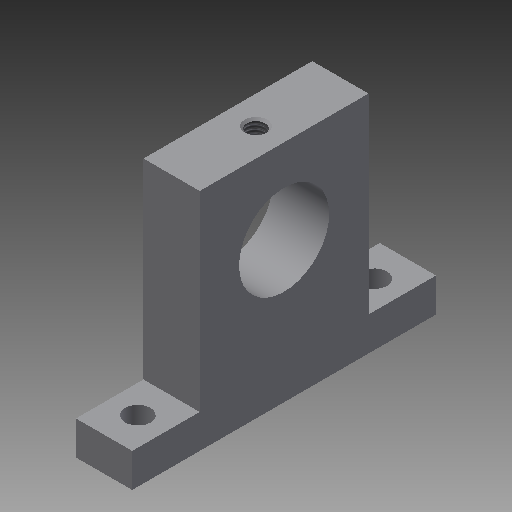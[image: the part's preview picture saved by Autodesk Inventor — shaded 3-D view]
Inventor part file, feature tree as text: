
AUTODESK INVENTOR PART (.ipt)
format: ipt  version: 2019 (Build 230136000, 136)  size: 129,536 bytes
history: native  units: mm
features: other x7, sketch x4, hole x3, extrude x1, pattern_linear x1
ambient origin geometry x8: Origin, YZ Plane, XZ Plane, XY Plane, X Axis, Y Axis, Z Axis, Center Point
bodies: Solid1 (feature_tree)
feature tree (16):
  extrude  "Extrusion1"  Depth=10.0mm TaperAngle=0.0deg
  hole  "Hole1"  [1 undecoded]
  hole  "Hole2"  [1 undecoded]
  pattern_linear  "Rectangular Pattern1"  [2 undecoded]
  hole  "Hole3"  [1 undecoded]
  other  "b_s_XY"
  other  "b_s_YZ"
  other  "b_s_ZX"
  other  "b_s_X"
  other  "b_s_Y"
  other  "b_s_Z"
  other  "b_s_Center"
  sketch  "Sketch_1"  dims[d0=10.0mm d1=0.0mm]
  sketch  "Sketch2"  dims[d2=3.242mm d3=7.379mm d4=4.0mm d5=2.0mm d6=90.0deg d7=14.064115mm d8=120.0deg]
  sketch  "Sketch3"  dims[d9=4.5mm d10=6.0mm d11=4.0mm d12=2.0mm d13=90.0deg d14=6.0mm d15=0.0mm d16=20.0mm d18=42.0mm d19=10.0mm d21=0.0mm]
  sketch  "Sketch4"  dims[d22=16.0mm d23=6.0mm d24=4.0mm d25=2.0mm d26=90.0deg d27=10.0mm d28=0.0mm]
note: 5 required parameter values undecoded (feature->parameter linkage not recoverable at this tier; creation-order binding heuristic only, values carry confidence <= 0.55)
